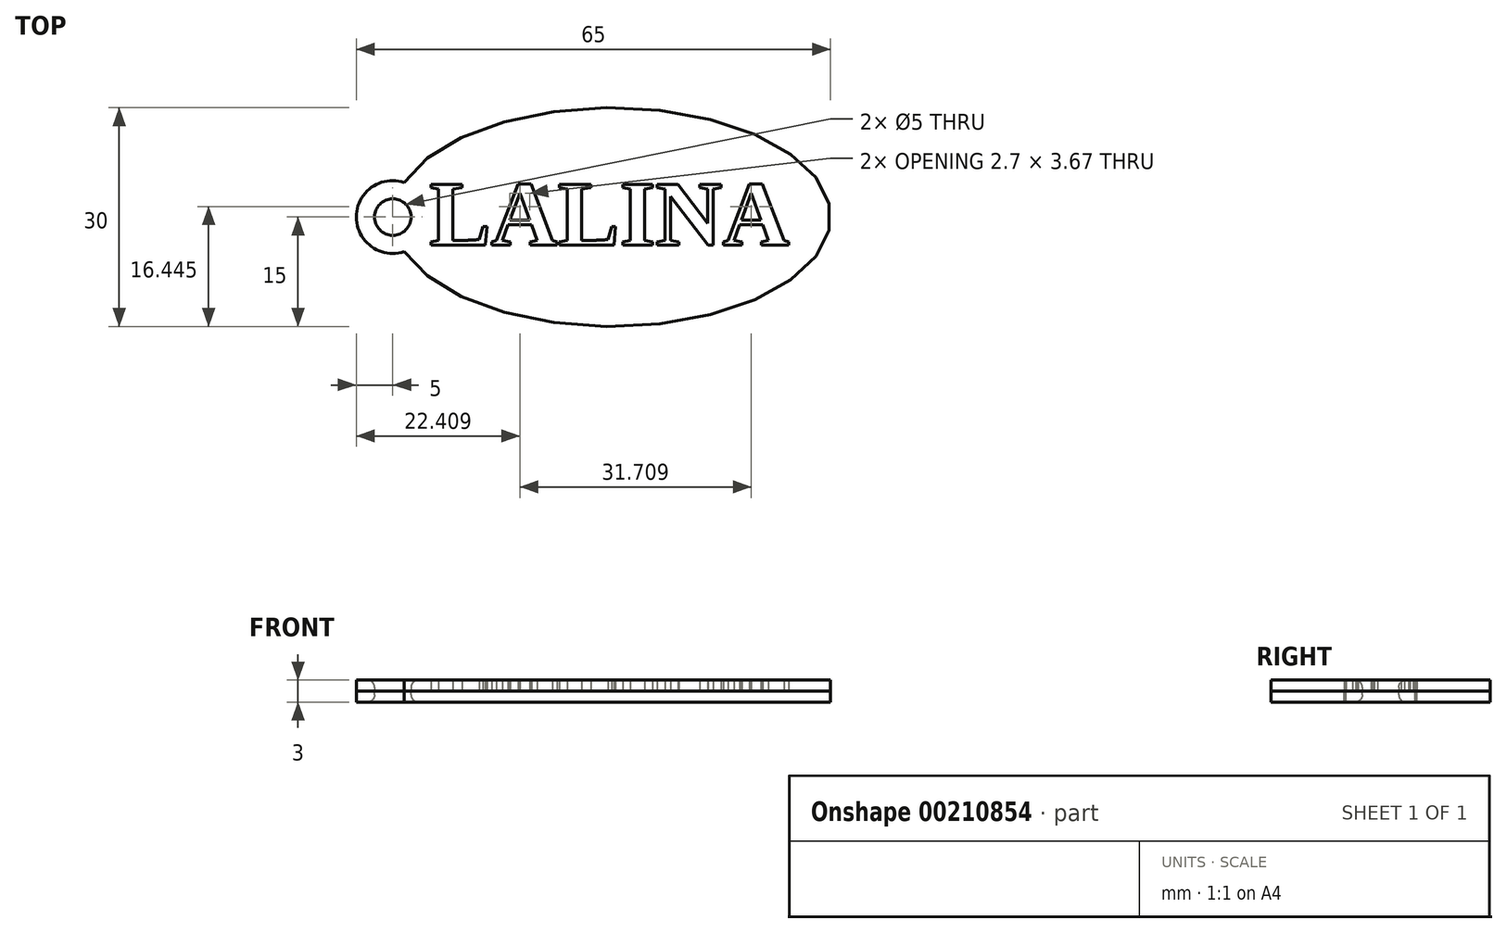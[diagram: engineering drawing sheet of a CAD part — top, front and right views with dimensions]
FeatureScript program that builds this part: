
annotation { "Feature Type Name" : "Feature", "Feature Type Description" : "" }
export const myFeature = defineFeature(function(context is Context, id is Id, definition is map)
    precondition{}
    {
        {
            var Q0;
            Q0=qCreatedBy(makeId("Top.planeOp"),FACE);
            var sketch = newSketch(context, id + "F0", { "sketchPlane" : qUnion([Q0])});
            skEllipse(sketch, "E0", {"center": v(0, 0) * mm, "majorRadius": 30 * mm, "minorRadius": 15 * mm, "majorAxis": v(1, 0)});
            skCircle(sketch, "E1", {"center": v(-30, 0) * mm, "radius": 5 * mm});
            skFitSpline(sketch, "E2.0", {"points": [v(27.93, -1.1) * mm, v(28.04, 0) * mm, v(27.93, 1.1) * mm, v(27.6, 2.2) * mm, v(27.04, 3.32) * mm, v(26.22, 4.46) * mm, v(25.14, 5.6) * mm, v(23.8, 6.73) * mm, v(22.47, 7.63) * mm, v(21.28, 8.32) * mm, v(20.33, 8.82) * mm, v(19.32, 9.3) * mm, v(17.91, 9.9) * mm, v(16.04, 10.6) * mm, v(13.63, 11.32) * mm, v(11.1, 11.92) * mm, v(8.44, 12.4) * mm, v(5.7, 12.74) * mm, v(3.34, 12.92) * mm, v(1.44, 12.99) * mm, v(0, 13) * mm, v(-1.44, 12.99) * mm, v(-3.34, 12.92) * mm, v(-5.7, 12.74) * mm, v(-8.44, 12.4) * mm, v(-11.1, 11.92) * mm, v(-13.63, 11.32) * mm, v(-16.04, 10.6) * mm, v(-17.91, 9.9) * mm, v(-19.32, 9.3) * mm, v(-20.33, 8.82) * mm, v(-21.28, 8.32) * mm, v(-22.47, 7.63) * mm, v(-23.8, 6.73) * mm, v(-25.14, 5.6) * mm, v(-26.22, 4.46) * mm, v(-27.04, 3.32) * mm, v(-27.6, 2.2) * mm, v(-27.93, 1.1) * mm, v(-28.04, 0) * mm, v(-27.93, -1.1) * mm, v(-27.6, -2.2) * mm, v(-27.04, -3.32) * mm, v(-26.22, -4.46) * mm, v(-25.14, -5.6) * mm, v(-23.8, -6.73) * mm, v(-22.47, -7.63) * mm, v(-21.28, -8.32) * mm, v(-20.33, -8.82) * mm, v(-19.32, -9.3) * mm, v(-17.91, -9.9) * mm, v(-16.04, -10.6) * mm, v(-13.63, -11.32) * mm, v(-11.1, -11.92) * mm, v(-8.44, -12.4) * mm, v(-5.7, -12.74) * mm, v(-3.34, -12.92) * mm, v(-1.44, -12.99) * mm, v(0, -13) * mm, v(1.44, -12.99) * mm, v(3.34, -12.92) * mm, v(5.7, -12.74) * mm, v(8.44, -12.4) * mm, v(11.1, -11.92) * mm, v(13.63, -11.32) * mm, v(16.04, -10.6) * mm, v(17.91, -9.9) * mm, v(19.32, -9.3) * mm, v(20.33, -8.82) * mm, v(21.28, -8.32) * mm, v(22.47, -7.63) * mm, v(23.8, -6.73) * mm, v(25.14, -5.6) * mm, v(26.22, -4.46) * mm, v(27.04, -3.32) * mm, v(27.6, -2.2) * mm, v(27.93, -1.1) * mm, v(28.04, 0) * mm, v(27.93, 1.1) * mm, v(27.93, -1.1) * mm]});
            skCircle(sketch, "E3", {"center": v(-30, 0) * mm, "radius": 2.5 * mm});
            skSolve(sketch);
        }
        {
            var Q0;
            Q0=qCreatedBy(makeId("Top.planeOp"),FACE);
            var sketch = newSketch(context, id + "F1", { "sketchPlane" : qUnion([Q0])});
            skText(sketch, "E4", { "text": "LALINA", "fontName": "Tinos-Bold.ttf"});
            const initialGuessF1  = {"E4": [-0.025, -0.00384, 1, 0, 0.00913]};
            skSetInitialGuess(sketch, initialGuessF1);
            skSolve(sketch);
        }
        {
            var Q0;
            {var subQ0=sQuery(id+"F0.wireOp",EDGE,"E1");var subQ1=sQuery(id+"F0.wireOp",EDGE,"E0");var subQ2=makeQuery(id+"F0.imprint","INTERSECT",VERTEX,{"disambiguationData":[OD(0.0)],"derivedFrom":[subQ1,subQ0]});Q0=makeQuery(id+"F0.imprint","IMPRINT",FACE,{"disambiguationData":[TD([[makeQuery(id+"F0.imprint","IMPRINT",EDGE,{"disambiguationData":[TD([[subQ2,1.0]])],"derivedFrom":subQ1}),1.0]])]});}
            var Q1;
            {var subQ0=sQuery(id+"F0.wireOp",EDGE,"E2.0");var subQ1=sQuery(id+"F0.wireOp",EDGE,"E1");var subQ2=makeQuery(id+"F0.imprint","INTERSECT",VERTEX,{"disambiguationData":[OD(0.0)],"derivedFrom":[subQ1,subQ0]});Q1=makeQuery(id+"F0.imprint","IMPRINT",FACE,{"disambiguationData":[TD([[makeQuery(id+"F0.imprint","IMPRINT",EDGE,{"disambiguationData":[TD([[subQ2,1.0]])],"derivedFrom":subQ1}),-1.0]])]});}
            var Q2;
            {var subQ0=sQuery(id+"F0.wireOp",EDGE,"E2.0");var subQ1=sQuery(id+"F0.wireOp",EDGE,"E1");var subQ2=makeQuery(id+"F0.imprint","INTERSECT",VERTEX,{"disambiguationData":[OD(0.0)],"derivedFrom":[subQ1,subQ0]});Q2=makeQuery(id+"F0.imprint","IMPRINT",FACE,{"disambiguationData":[TD([[makeQuery(id+"F0.imprint","IMPRINT",EDGE,{"disambiguationData":[TD([[subQ2,1.0]])],"derivedFrom":subQ1}),1.0]])]});}
            var Q3;
            {var subQ0=sQuery(id+"F0.wireOp",EDGE,"E1");var subQ1=sQuery(id+"F0.wireOp",EDGE,"E0");var subQ2=makeQuery(id+"F0.imprint","INTERSECT",VERTEX,{"disambiguationData":[OD(0.0)],"derivedFrom":[subQ1,subQ0]});Q3=makeQuery(id+"F0.imprint","IMPRINT",FACE,{"disambiguationData":[TD([[makeQuery(id+"F0.imprint","IMPRINT",EDGE,{"disambiguationData":[TD([[subQ2,-1.0]])],"derivedFrom":subQ1}),-1.0]])]});}
            var Q4;
            {var subQ0=sQuery(id+"F0.wireOp",EDGE,"E1");var subQ1=sQuery(id+"F0.wireOp",EDGE,"E0");var subQ2=makeQuery(id+"F0.imprint","INTERSECT",VERTEX,{"disambiguationData":[OD(0.0)],"derivedFrom":[subQ1,subQ0]});Q4=makeQuery(id+"F0.imprint","IMPRINT",FACE,{"disambiguationData":[TD([[makeQuery(id+"F0.imprint","IMPRINT",EDGE,{"disambiguationData":[TD([[subQ2,-1.0]])],"derivedFrom":subQ1}),1.0]])]});}
            var Q5;
            {var subQ0=sQuery(id+"F0.wireOp",EDGE,"E1");var subQ1=sQuery(id+"F0.wireOp",EDGE,"E0");var subQ2=makeQuery(id+"F0.imprint","INTERSECT",VERTEX,{"disambiguationData":[OD(1.0)],"derivedFrom":[subQ1,subQ0]});Q5=makeQuery(id+"F0.imprint","IMPRINT",FACE,{"disambiguationData":[TD([[makeQuery(id+"F0.imprint","IMPRINT",EDGE,{"disambiguationData":[TD([[subQ2,1.0]])],"derivedFrom":subQ1}),1.0]])]});}
            extrude(context, id + "F2", {"entities" : qUnion([Q0, Q1, Q2, Q3, Q4, Q5]), "oppositeDirection" : true, "depth" : 1.5 * mm, "offsetDistance" : 25 * mm});
        }
        {
            var Q0;
            {var subQ0=sQuery(id+"F0.wireOp",EDGE,"E1");var subQ1=sQuery(id+"F0.wireOp",EDGE,"E0");var subQ2=makeQuery(id+"F0.imprint","INTERSECT",VERTEX,{"disambiguationData":[OD(0.0)],"derivedFrom":[subQ1,subQ0]});Q0=makeQuery(id+"F0.imprint","IMPRINT",FACE,{"disambiguationData":[TD([[makeQuery(id+"F0.imprint","IMPRINT",EDGE,{"disambiguationData":[TD([[subQ2,1.0]])],"derivedFrom":subQ1}),1.0]])]});}
            var Q1;
            {var subQ0=sQuery(id+"F0.wireOp",EDGE,"E1");var subQ1=sQuery(id+"F0.wireOp",EDGE,"E0");var subQ2=makeQuery(id+"F0.imprint","INTERSECT",VERTEX,{"disambiguationData":[OD(0.0)],"derivedFrom":[subQ1,subQ0]});Q1=makeQuery(id+"F0.imprint","IMPRINT",FACE,{"disambiguationData":[TD([[makeQuery(id+"F0.imprint","IMPRINT",EDGE,{"disambiguationData":[TD([[subQ2,-1.0]])],"derivedFrom":subQ1}),-1.0]])]});}
            var Q2;
            {var subQ0=sQuery(id+"F0.wireOp",EDGE,"E2.0");var subQ1=sQuery(id+"F0.wireOp",EDGE,"E1");var subQ2=makeQuery(id+"F0.imprint","INTERSECT",VERTEX,{"disambiguationData":[OD(0.0)],"derivedFrom":[subQ1,subQ0]});Q2=makeQuery(id+"F0.imprint","IMPRINT",FACE,{"disambiguationData":[TD([[makeQuery(id+"F0.imprint","IMPRINT",EDGE,{"disambiguationData":[TD([[subQ2,1.0]])],"derivedFrom":subQ1}),1.0]])]});}
            var Q3;
            {var subQ0=sQuery(id+"F0.wireOp",EDGE,"E1");var subQ1=sQuery(id+"F0.wireOp",EDGE,"E0");var subQ2=makeQuery(id+"F0.imprint","INTERSECT",VERTEX,{"disambiguationData":[OD(0.0)],"derivedFrom":[subQ1,subQ0]});Q3=makeQuery(id+"F0.imprint","IMPRINT",FACE,{"disambiguationData":[TD([[makeQuery(id+"F0.imprint","IMPRINT",EDGE,{"disambiguationData":[TD([[subQ2,-1.0]])],"derivedFrom":subQ1}),1.0]])]});}
            var Q4;
            {var subQ0=sQuery(id+"F0.wireOp",EDGE,"E1");var subQ1=sQuery(id+"F0.wireOp",EDGE,"E0");var subQ2=makeQuery(id+"F0.imprint","INTERSECT",VERTEX,{"disambiguationData":[OD(1.0)],"derivedFrom":[subQ1,subQ0]});Q4=makeQuery(id+"F0.imprint","IMPRINT",FACE,{"disambiguationData":[TD([[makeQuery(id+"F0.imprint","IMPRINT",EDGE,{"disambiguationData":[TD([[subQ2,1.0]])],"derivedFrom":subQ1}),1.0]])]});}
            var Q5;
            Q5=qSketchRegion(id+"F1",true);
            extrude(context, id + "F3", {"entities" : qUnion([Q0, Q1, Q2, Q3, Q4, Q5]), "depth" : 1.5 * mm, "offsetDistance" : 25 * mm});
        }
        {
            var Q0;
            Q0=makeQuery(id+"F3.opExtrude","CAP_EDGE",EDGE,{"disambiguationData":[OSD([sQuery(id+"F0.wireOp",EDGE,"E3")])],"isStart":false});
            var Q1;
            Q1=makeQuery(id+"F2.opExtrude","CAP_EDGE",EDGE,{"disambiguationData":[OSD([sQuery(id+"F0.wireOp",EDGE,"E3")])],"isStart":false});
            fillet(context, id + "F4", {"entities" : qUnion([Q0, Q1]), "radius" : 1 * mm, "tangentPropagation" : true, "allowEdgeOverflow" : false});
        }
    });
